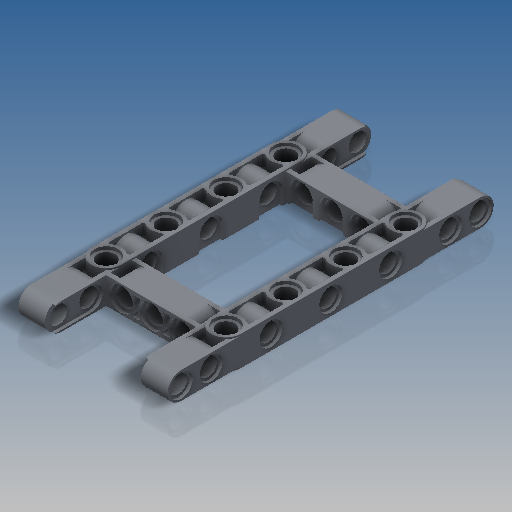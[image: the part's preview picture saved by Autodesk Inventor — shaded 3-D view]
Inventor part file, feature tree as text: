
AUTODESK INVENTOR PART (.ipt)
format: ipt  version: 2018.3 (Build 223284000, 284)  size: 1,127,424 bytes
history: native  units: mm
features: extrude x16, sketch x7, mirror x4, fillet x3, plane x1, projected_geometry x1
ambient origin geometry x8: Origin, YZ Plane, XZ Plane, XY Plane, X Axis, Y Axis, Z Axis, Center Point
bodies: Solid1 (feature_tree)
feature tree (32):
  sketch  "Sketch1"  dims[d14=8.0mm d15=0.0mm d32=8.0mm]
  extrude  "Extrusion1"  Depth=8.0mm
  extrude  "Extrusion18"  Depth=0.8mm TaperAngle=0.0deg
  sketch  "Sketch6"  dims[d41=0.8mm d42=0.0mm d43=3.1mm d44=0.0mm]
  extrude  "Extrusion7"  Depth=6.4mm
  extrude  "Extrusion8"  Depth=16.0mm
  mirror  "Mirror1"
  extrude  "Extrusion19"  Depth=7.2mm
  extrude  "Extrusion9"  Depth=10.0mm TaperAngle=0.0deg
  extrude  "Extrusion10"  Depth=0.8mm TaperAngle=0.0deg
  extrude  "Extrusion11"  [1 undecoded]
  mirror  "Mirror2"
  extrude  "Extrusion26"  Depth=10.0mm TaperAngle=0.0deg
  extrude  "Extrusion20"  Depth=10.0mm
  fillet  "Fillet2"  Radius=16.0mm
  plane  "Work Plane1"
  extrude  "Extrusion13"  Depth=7.2mm
  sketch  "Sketch16"  dims[d69=7.2mm d70=4.8mm]
  extrude  "Extrusion21"  TaperAngle=0.0deg  [1 undecoded]
  extrude  "Extrusion22"  Depth=8.0mm
  extrude  "Extrusion23"  Depth=6.4mm
  extrude  "Extrusion24"  Depth=10.0mm
  extrude  "Extrusion25"  Depth=7.2mm
  fillet  "Fillet3"  [1 undecoded]
  mirror  "Mirror5"
  mirror  "Mirror3"
  fillet  "Fillet4"  Radius=7.2mm
  projected_geometry  "Projected Loop4"
  sketch  "Sketch8"  dims[d49=6.4mm d50=4.8mm]
  sketch  "Sketch15"  dims[d60=0.4mm d61=0.1mm d62=30.0mm d64=16.0mm d65=10.0mm d67=10.0mm]
  sketch  "Sketch17"  dims[d71=10.0mm d72=0.0mm d73=10.0mm d74=0.0mm]
  sketch  "Sketch18"  dims[d75=6.2mm d76=0.8mm d77=0.0mm d78=-16.0mm d90=0.9mm d91=0.0mm d104=0.4mm d105=16.0mm d106=7.2mm d107=0.0mm d108=8.0mm d109=6.4mm d110=4.8mm d111=7.2mm d112=0.0mm d113=7.2mm d114=0.0mm d115=8.0mm d116=45.0deg d117=8.0mm d118=4.8mm d119=6.4mm d120=7.2mm d121=0.0mm d122=7.2mm d123=0.0mm d124=0.8mm d125=0.0mm d126=45.0deg d127=6.2mm d128=0.0mm d129=6.4mm d130=0.8mm d131=0.0mm d132=0.1mm d133=10.0mm d134=0.0mm]
note: 3 required parameter values undecoded (feature->parameter linkage not recoverable at this tier; creation-order binding heuristic only, values carry confidence <= 0.55)
